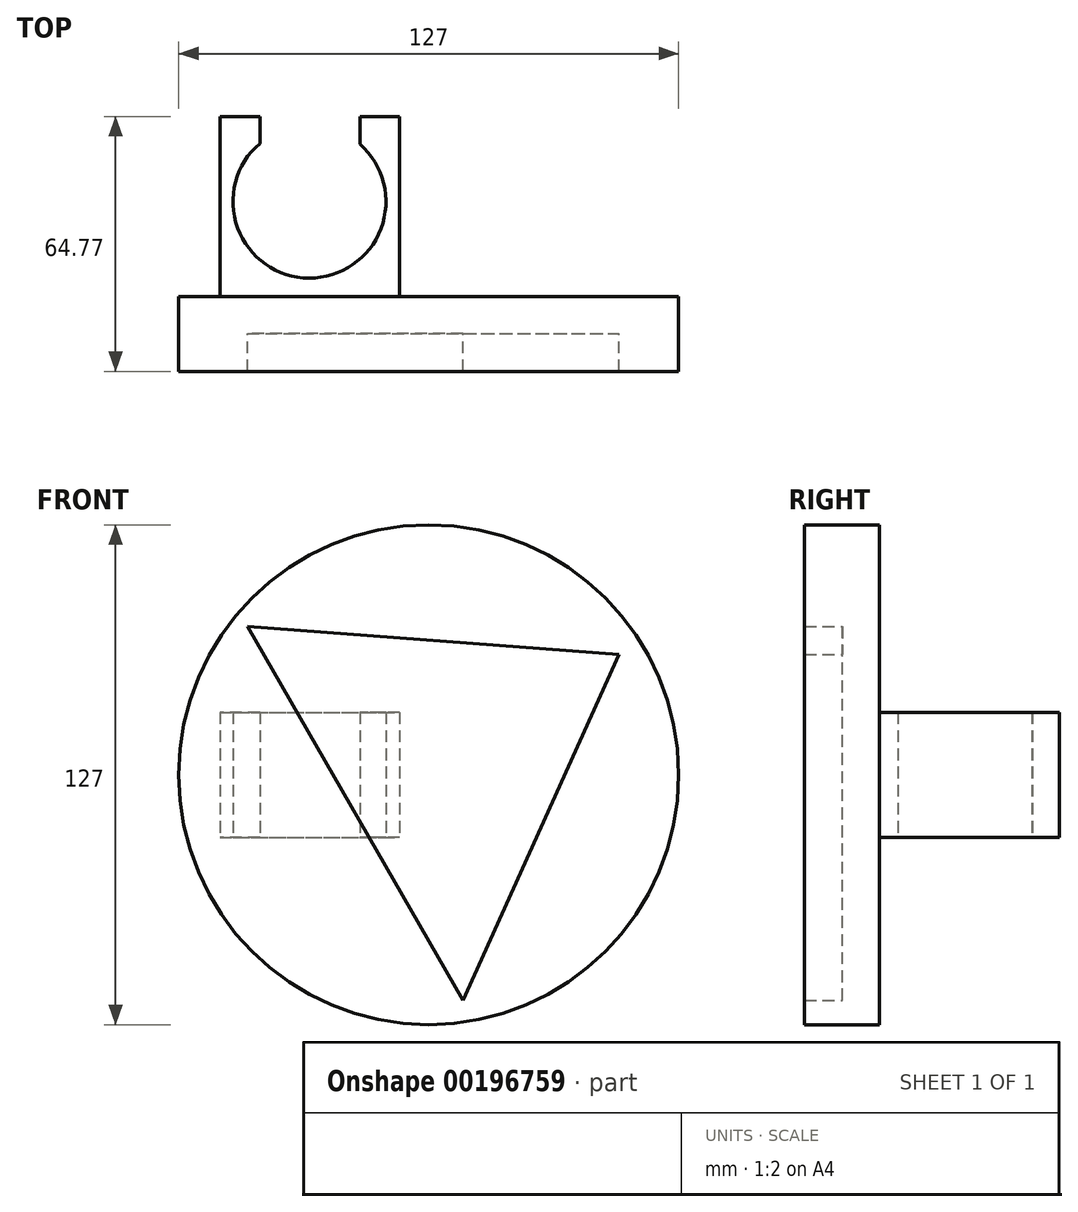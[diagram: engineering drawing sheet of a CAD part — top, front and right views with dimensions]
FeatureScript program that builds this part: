
annotation { "Feature Type Name" : "Feature", "Feature Type Description" : "" }
export const myFeature = defineFeature(function(context is Context, id is Id, definition is map)
    precondition{}
    {
        {
            var Q0;
            Q0=qCreatedBy(makeId("Front.planeOp"),FACE);
            var sketch = newSketch(context, id + "F0", { "sketchPlane" : qUnion([Q0])});
            skCircle(sketch, "E0", {"center": v(0, 0) * mm, "radius": 63.5 * mm});
            skLineSegment(sketch, "E1", {"start": v(-46.07, 37.63) * mm, "end": v(48.39, 30.55) * mm});
            skPoint(sketch, "E2.orphan", {"position": v(19.26, 120.55) * mm});
            skLineSegment(sketch, "E3", {"start": v(8.74, -57.3) * mm, "end": v(48.39, 30.55) * mm});
            skLineSegment(sketch, "E4", {"start": v(8.74, -57.3) * mm, "end": v(-46.07, 37.63) * mm});
            skSolve(sketch);
        }
        {
            var Q0;
            Q0=qSketchRegion(id+"F0",true);
            extrude(context, id + "F1", {"entities" : qUnion([Q0]), "depth" : 19.05 * mm});
        }
        {
            var Q0;
            Q0=qCreatedBy(makeId("Front.planeOp"),FACE);
            var sketch = newSketch(context, id + "F2", { "sketchPlane" : qUnion([Q0])});
            skLineSegment(sketch, "E5", {"start": v(-45.18, 38.8) * mm, "end": v(49.28, 31.8) * mm});
            skPoint(sketch, "E6.orphan", {"position": v(-37.57, 47.7) * mm});
            skLineSegment(sketch, "E7", {"start": v(9.72, -56.08) * mm, "end": v(49.28, 31.8) * mm});
            skLineSegment(sketch, "E8", {"start": v(9.72, -56.08) * mm, "end": v(-45.18, 38.8) * mm});
            skSolve(sketch);
        }
        {
            var Q0;
            Q0=makeQuery(id+"F0.imprint","IMPRINT",FACE,{"disambiguationData":[TD([[makeQuery(id+"F0.imprint","IMPRINT",EDGE,{"derivedFrom":sQuery(id+"F0.wireOp",EDGE,"E1")}),-1.0]])]});
            extrude(context, id + "F3", {"entities" : qUnion([Q0]), "operationType" : NewBodyOperationType.ADD, "depth" : 9.4 * mm});
        }
        {
            var Q0;
            Q0=qCreatedBy(makeId("Top.planeOp"),FACE);
            var sketch = newSketch(context, id + "F4", { "sketchPlane" : qUnion([Q0])});
            skLineSegment(sketch, "E9.MirrorCS", {"start": v(-7.33, 0) * mm, "end": v(-7.33, 45.72) * mm});
            skArc(sketch, "E10.MirrorCS", {"start": v(-42.9, 38.84) * mm, "mid": v(-30.41, 4.62) * mm, "end": v(-17.5, 38.68) * mm});
            skLineSegment(sketch, "E11.MirrorCS", {"start": v(-53.05, 0) * mm, "end": v(-53.05, 45.72) * mm});
            skLineSegment(sketch, "E12.MirrorCS", {"start": v(-42.9, 45.72) * mm, "end": v(-53.05, 45.72) * mm});
            skLineSegment(sketch, "E13.MirrorCS", {"start": v(-42.9, 45.72) * mm, "end": v(-42.9, 38.84) * mm});
            skLineSegment(sketch, "E14.MirrorCS", {"start": v(-17.5, 38.68) * mm, "end": v(-17.5, 45.72) * mm});
            skLineSegment(sketch, "E15.MirrorCS", {"start": v(-7.33, 45.72) * mm, "end": v(-17.5, 45.72) * mm});
            skLineSegment(sketch, "E16.MirrorCS", {"start": v(-53.05, 0) * mm, "end": v(-7.33, 0) * mm});
            skSolve(sketch);
        }
        {
            var Q0;
            Q0=qSketchRegion(id+"F4",true);
            extrude(context, id + "F5", {"entities" : qUnion([Q0]), "operationType" : NewBodyOperationType.ADD, "endBound" : BoundingType.SYMMETRIC, "depth" : 31.75 * mm});
        }
        {
            var Q0;
            Q0 = qSketchRegion(id + "F2", true);
            extrude(context, id + "F6", {"entities" : qUnion([Q0]), "operationType" : NewBodyOperationType.ADD, "depth" : 6.35 * mm});
        }
    });
